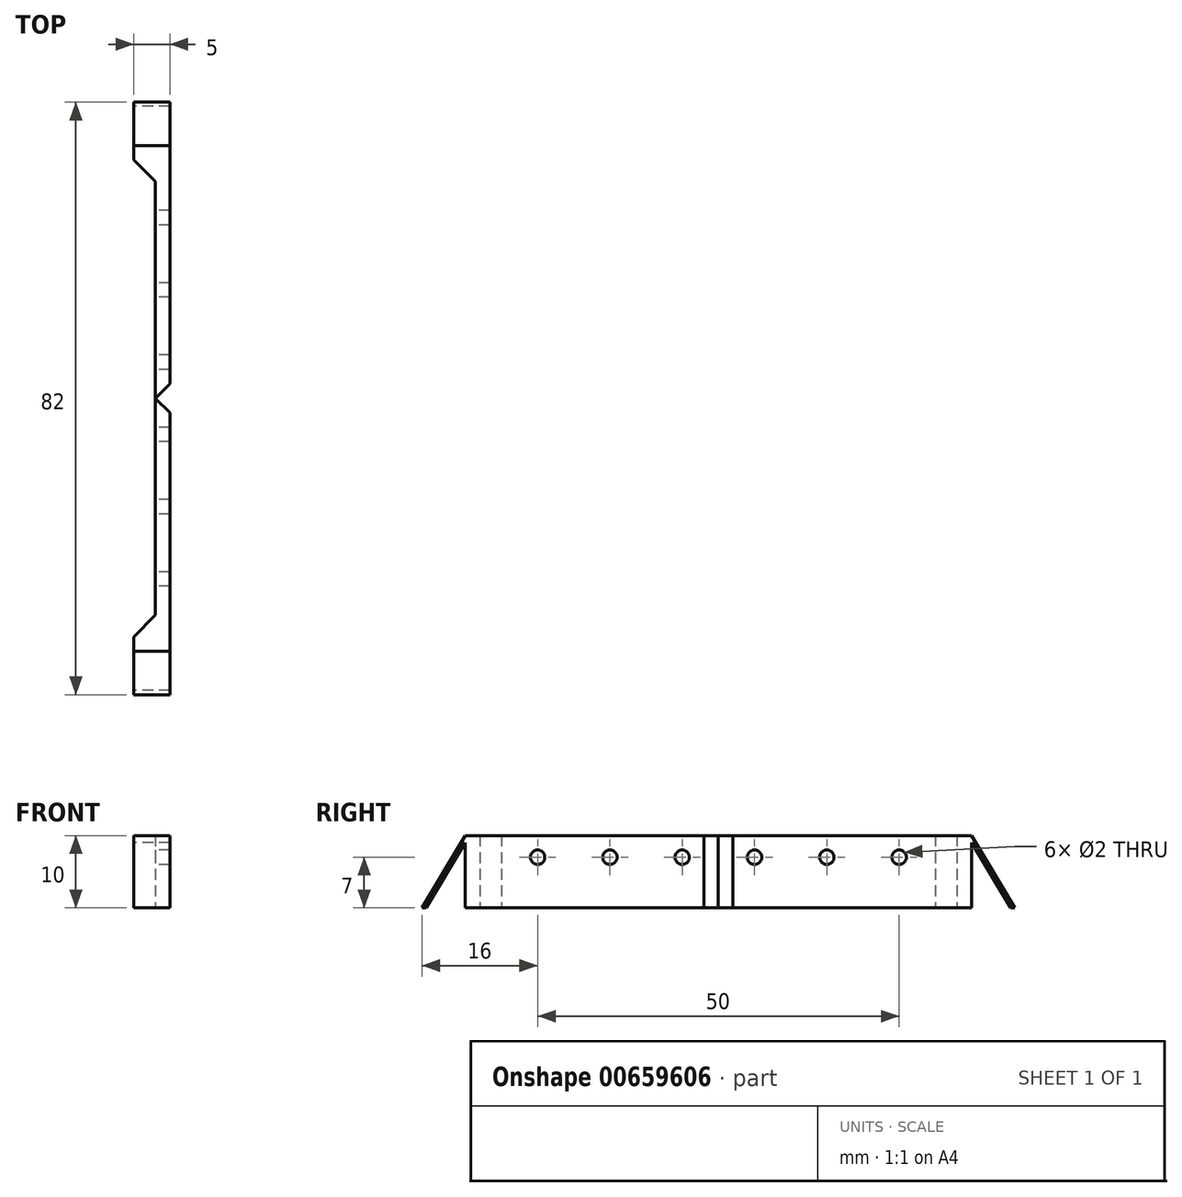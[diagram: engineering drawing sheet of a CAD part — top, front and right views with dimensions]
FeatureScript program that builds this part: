
annotation { "Feature Type Name" : "Feature", "Feature Type Description" : "" }
export const myFeature = defineFeature(function(context is Context, id is Id, definition is map)
    precondition{}
    {
        {
            var Q0;
            Q0=qCreatedBy(makeId("Top.planeOp"),FACE);
            var sketch = newSketch(context, id + "F0", { "sketchPlane" : qUnion([Q0])});
            skLineSegment(sketch, "E0.bottom", {"start": v(20, -19.5) * mm, "end": v(-20, -19.5) * mm});
            skLineSegment(sketch, "E0.top", {"start": v(20, 19.5) * mm, "end": v(-20, 19.5) * mm});
            skLineSegment(sketch, "E0.left", {"start": v(20, -19.5) * mm, "end": v(20, 19.5) * mm});
            skLineSegment(sketch, "E0.right", {"start": v(-20, -19.5) * mm, "end": v(-20, 19.5) * mm});
            skPoint(sketch, "E0.middle", {"position": v(0, 0) * mm});
            skLineSegment(sketch, "E1.0", {"start": v(22, -21.5) * mm, "end": v(-22, -21.5) * mm});
            skLineSegment(sketch, "E1.1", {"start": v(22, -21.5) * mm, "end": v(22, 21.5) * mm});
            skLineSegment(sketch, "E1.2", {"start": v(22, 21.5) * mm, "end": v(-22, 21.5) * mm});
            skLineSegment(sketch, "E1.3", {"start": v(-22, -21.5) * mm, "end": v(-22, 21.5) * mm});
            skLineSegment(sketch, "E2", {"start": v(-20, -19.5) * mm, "end": v(-22, -19.5) * mm});
            skLineSegment(sketch, "E3", {"start": v(20, 19.5) * mm, "end": v(20, 21.5) * mm});
            skSolve(sketch);
        }
        {
            var Q0;
            Q0=makeQuery(id+"F0.imprint","IMPRINT",FACE,{"disambiguationData":[TD([[makeQuery(id+"F0.imprint","IMPRINT",EDGE,{"derivedFrom":sQuery(id+"F0.wireOp",EDGE,"E0.top")}),-1.0]])]});
            var Q1;
            Q1=makeQuery(id+"F0.imprint","IMPRINT",FACE,{"disambiguationData":[TD([[makeQuery(id+"F0.imprint","IMPRINT",EDGE,{"derivedFrom":sQuery(id+"F0.wireOp",EDGE,"E0.bottom")}),1.0]])]});
            extrude(context, id + "F1", {"entities" : qUnion([Q0, Q1]), "oppositeDirection" : true, "depth" : 10 * mm, "offsetDistance" : 25 * mm});
        }
        {
            var Q0;
            Q0=makeQuery(id+"F1.opExtrude","SWEPT_FACE",FACE,{"disambiguationData":[OSD([sQuery(id+"F0.wireOp",EDGE,"E1.3")])]});
            var sketch = newSketch(context, id + "F2", { "sketchPlane" : qUnion([Q0])});
            skLineSegment(sketch, "E4", {"start": v(13.5, 0) * mm, "end": v(19.5, -10) * mm});
            skLineSegment(sketch, "E5", {"start": v(19.5, -10) * mm, "end": v(18.92, -10) * mm});
            skLineSegment(sketch, "E6", {"start": v(18.92, -10) * mm, "end": v(13.5, -0.97) * mm});
            skLineSegment(sketch, "E7", {"start": v(13.5, -0.97) * mm, "end": v(13.5, -10) * mm});
            skLineSegment(sketch, "E8", {"start": v(19.5, -10) * mm, "end": v(19.5, 0) * mm});
            skLineSegment(sketch, "E9", {"start": v(19.5, 0) * mm, "end": v(13.5, 0) * mm});
            skSolve(sketch);
        }
        {
            var Q0;
            {var subQ0=sQuery(id+"F2.wireOp",EDGE,"E6");Q0=makeQuery(id+"F2.imprint","IMPRINT",FACE,{"disambiguationData":[TD([[makeQuery(id+"F2.imprint","IMPRINT",EDGE,{"derivedFrom":subQ0}),1.0]])]});}
            extrude(context, id + "F3", {"entities" : qUnion([Q0]), "operationType" : NewBodyOperationType.REMOVE, "oppositeDirection" : true, "depth" : 25 * mm, "offsetDistance" : 25 * mm});
        }
        {
            var Q0;
            Q0=makeQuery(id+"F2.imprint","IMPRINT",FACE,{"disambiguationData":[TD([[makeQuery(id+"F2.imprint","IMPRINT",EDGE,{"derivedFrom":sQuery(id+"F2.wireOp",EDGE,"E4")}),1.0]])]});
            extrude(context, id + "F4", {"entities" : qUnion([Q0]), "operationType" : NewBodyOperationType.REMOVE, "endBound" : BoundingType.THROUGH_ALL, "oppositeDirection" : true, "depth" : 2 * mm, "offsetDistance" : 25 * mm});
        }
        {
            var Q0;
            Q0=makeQuery(id+"F1.opExtrude","SWEPT_FACE",FACE,{"disambiguationData":[OSD([sQuery(id+"F0.wireOp",EDGE,"E1.2")])]});
            var sketch = newSketch(context, id + "F5", { "sketchPlane" : qUnion([Q0])});
            skLineSegment(sketch, "E10", {"start": v(-20, -10) * mm, "end": v(-14, -0.9) * mm});
            skLineSegment(sketch, "E11", {"start": v(-14, -0.9) * mm, "end": v(-14, -10) * mm});
            skLineSegment(sketch, "E12", {"start": v(-14, 0) * mm, "end": v(-20, -9.1) * mm});
            skLineSegment(sketch, "E13", {"start": v(-20, -9.1) * mm, "end": v(-20, -10) * mm});
            skSolve(sketch);
        }
        {
            var Q0;
            {var subQ0=sQuery(id+"F5.wireOp",EDGE,"E10");Q0=makeQuery(id+"F5.imprint","IMPRINT",FACE,{"disambiguationData":[TD([[makeQuery(id+"F5.imprint","IMPRINT",EDGE,{"derivedFrom":subQ0}),-1.0]])]});}
            var Q1;
            {var subQ3=sQuery(id+"F5.wireOp",EDGE,"E12");Q1=makeQuery(id+"F5.imprint","IMPRINT",FACE,{"disambiguationData":[TD([[makeQuery(id+"F5.imprint","IMPRINT",EDGE,{"derivedFrom":subQ3}),-1.0]])]});}
            extrude(context, id + "F6", {"entities" : qUnion([Q0, Q1]), "operationType" : NewBodyOperationType.REMOVE, "endBound" : BoundingType.THROUGH_ALL, "oppositeDirection" : true, "depth" : 25 * mm, "offsetDistance" : 25 * mm});
        }
        {
            var Q0;
            {var subQ0=sQuery(id+"F0.wireOp",EDGE,"E1.3");var subQ7=sQuery(id+"F0.wireOp",EDGE,"E0.bottom");Q0=makeQuery(id+"F4.boolean.opBoolean","SPLIT",FACE,{"disambiguationData":[TD([makeQuery(id+"F1.opExtrude","SWEPT_FACE",FACE,{"disambiguationData":[OSD([subQ7])]})])],"derivedFrom":makeQuery(id+"F1.opExtrude","SWEPT_FACE",FACE,{"disambiguationData":[OSD([subQ0])]})});}
            extrude(context, id + "F7", {"entities" : qUnion([Q0]), "operationType" : NewBodyOperationType.REMOVE, "endBound" : BoundingType.THROUGH_ALL, "oppositeDirection" : true, "depth" : 25 * mm, "offsetDistance" : 25 * mm});
        }
        {
            var Q0;
            Q0=makeQuery(id+"F1.opExtrude","SWEPT_FACE",FACE,{"disambiguationData":[OSD([sQuery(id+"F0.wireOp",EDGE,"E1.2")])]});
            var sketch = newSketch(context, id + "F8", { "sketchPlane" : qUnion([Q0])});
            skLineSegment(sketch, "E14", {"start": v(-9, -10) * mm, "end": v(-9, 0) * mm});
            skSolve(sketch);
        }
        {
            var Q0;
            {var subQ2=sQuery(id+"F8.wireOp",EDGE,"E14");Q0=makeQuery(id+"F8.imprint","IMPRINT",FACE,{"disambiguationData":[TD([[makeQuery(id+"F8.imprint","IMPRINT",EDGE,{"derivedFrom":subQ2}),1.0]])]});}
            extrude(context, id + "F9", {"entities" : qUnion([Q0]), "operationType" : NewBodyOperationType.ADD, "depth" : 3 * mm, "offsetDistance" : 25 * mm});
        }
        {
            var Q0;
            Q0=makeQuery(id+"F9.opExtrude","CAP_EDGE",EDGE,{"disambiguationData":[OSD([sQuery(id+"F8.wireOp",EDGE,"E14")])],"isStart":false});
            chamfer(context, id + "F10", {"entities" : qUnion([Q0]), "width" : 3 * mm, "tangentPropagation" : true});
        }
        {
            var Q0;
            {var subQ0=sQuery(id+"F0.wireOp",EDGE,"E1.2");var subQ1=sQuery(id+"F0.wireOp",EDGE,"E1.3");Q0=makeQuery(id+"F4.boolean.opBoolean","SPLIT",FACE,{"disambiguationData":[TD([makeQuery(id+"F1.opExtrude","SWEPT_FACE",FACE,{"disambiguationData":[OSD([subQ0])]})])],"derivedFrom":makeQuery(id+"F1.opExtrude","SWEPT_FACE",FACE,{"disambiguationData":[OSD([subQ1])]})});}
            var sketch = newSketch(context, id + "F11", { "sketchPlane" : qUnion([Q0])});
            skLineSegment(sketch, "E15", {"start": v(8.5, 0) * mm, "end": v(8.5, -10) * mm});
            skSolve(sketch);
        }
        {
            var Q0;
            {var subQ5=sQuery(id+"F11.wireOp",EDGE,"E15");Q0=makeQuery(id+"F11.imprint","IMPRINT",FACE,{"disambiguationData":[TD([[makeQuery(id+"F11.imprint","IMPRINT",EDGE,{"derivedFrom":subQ5}),1.0]])]});}
            extrude(context, id + "F12", {"entities" : qUnion([Q0]), "operationType" : NewBodyOperationType.ADD, "depth" : 3 * mm, "offsetDistance" : 25 * mm});
        }
        {
            var Q0;
            Q0=makeQuery(id+"F12.opExtrude","CAP_EDGE",EDGE,{"disambiguationData":[OSD([sQuery(id+"F11.wireOp",EDGE,"E15")])],"isStart":false});
            chamfer(context, id + "F13", {"entities" : qUnion([Q0]), "width" : 3 * mm, "tangentPropagation" : true});
        }
        {
            var Q0;
            {var subQ0=sQuery(id+"F0.wireOp",EDGE,"E1.2");var subQ1=sQuery(id+"F0.wireOp",EDGE,"E1.3");Q0=makeQuery(id+"F4.boolean.opBoolean","SPLIT",FACE,{"disambiguationData":[TD([makeQuery(id+"F1.opExtrude","SWEPT_FACE",FACE,{"disambiguationData":[OSD([subQ0])]})])],"derivedFrom":makeQuery(id+"F1.opExtrude","SWEPT_FACE",FACE,{"disambiguationData":[OSD([subQ1])]})});}
            var sketch = newSketch(context, id + "F14", { "sketchPlane" : qUnion([Q0])});
            skLineSegment(sketch, "E16", {"start": v(-6.5, -10) * mm, "end": v(-6.5, -3) * mm, "construction": true});
            skPoint(sketch, "E16.endSnap0", {"position": v(-6.5, -10) * mm});
            skLineSegment(sketch, "E17", {"start": v(-6.5, -3) * mm, "end": v(3.5, -3) * mm, "construction": true});
            skLineSegment(sketch, "E18", {"start": v(-6.5, -3) * mm, "end": v(-16.5, -3) * mm, "construction": true});
            skSolve(sketch);
        }
        {
            var Q0;
            Q0=makeQuery(id+"F1.opExtrude","SWEPT_FACE",FACE,{"disambiguationData":[OSD([sQuery(id+"F0.wireOp",EDGE,"E1.2")])]});
            var sketch = newSketch(context, id + "F15", { "sketchPlane" : qUnion([Q0])});
            skLineSegment(sketch, "E19", {"start": v(6.5, -3) * mm, "end": v(16.5, -3) * mm, "construction": true});
            skPoint(sketch, "E19.startSnap0", {"position": v(6.5, -10) * mm});
            skLineSegment(sketch, "E20", {"start": v(6.5, -3) * mm, "end": v(-3.5, -3) * mm, "construction": true});
            skLineSegment(sketch, "E21", {"start": v(6.5, -3) * mm, "end": v(6.5, -10) * mm, "construction": true});
            skSolve(sketch);
        }
        {
            var Q0;
            Q0=sQuery(id+"F14.wireOp",VERTEX,"E18.start");
            var Q1;
            Q1=sQuery(id+"F14.wireOp",VERTEX,"E17.end");
            var Q2;
            Q2=sQuery(id+"F14.wireOp",VERTEX,"E18.end");
            var Q3;
            Q3=makeQuery(id+"F4.boolean.opBoolean","SPLIT",BODY,{"disambiguationData":[OD(1.0)],"derivedFrom":makeQuery(id+"F1.opExtrude","SWEPT_BODY",BODY,{"disambiguationData":[OSD([sQuery(id+"F0.wireOp",EDGE,"E0.bottom"),sQuery(id+"F0.wireOp",EDGE,"E0.top"),sQuery(id+"F0.wireOp",EDGE,"E0.left"),sQuery(id+"F0.wireOp",EDGE,"E0.right"),sQuery(id+"F0.wireOp",EDGE,"E1.0"),sQuery(id+"F0.wireOp",EDGE,"E1.1"),sQuery(id+"F0.wireOp",EDGE,"E1.2"),sQuery(id+"F0.wireOp",EDGE,"E1.3")])]})});
            hole(context, id + "F16", {"style" : HoleStyle.SIMPLE, "endStyle" : HoleEndStyle.THROUGH, "holeDiameter" : 2 * mm, "majorDiameter" : 5 * mm, "isTappedThrough" : true, "tappedDepth" : 12 * mm, "tapClearance" : 3, "locations" : qUnion([Q0, Q1, Q2]), "scope" : qUnion([Q3])});
        }
        {
            var Q0;
            Q0=sQuery(id+"F15.wireOp",VERTEX,"E20.end");
            var Q1;
            Q1=sQuery(id+"F15.wireOp",VERTEX,"E19.start");
            var Q2;
            Q2=sQuery(id+"F15.wireOp",VERTEX,"E19.end");
            var Q3;
            Q3=makeQuery(id+"F4.boolean.opBoolean","SPLIT",BODY,{"disambiguationData":[OD(1.0)],"derivedFrom":makeQuery(id+"F1.opExtrude","SWEPT_BODY",BODY,{"disambiguationData":[OSD([sQuery(id+"F0.wireOp",EDGE,"E0.bottom"),sQuery(id+"F0.wireOp",EDGE,"E0.top"),sQuery(id+"F0.wireOp",EDGE,"E0.left"),sQuery(id+"F0.wireOp",EDGE,"E0.right"),sQuery(id+"F0.wireOp",EDGE,"E1.0"),sQuery(id+"F0.wireOp",EDGE,"E1.1"),sQuery(id+"F0.wireOp",EDGE,"E1.2"),sQuery(id+"F0.wireOp",EDGE,"E1.3")])]})});
            hole(context, id + "F17", {"style" : HoleStyle.SIMPLE, "endStyle" : HoleEndStyle.THROUGH, "holeDiameter" : 2 * mm, "majorDiameter" : 5 * mm, "isTappedThrough" : true, "tappedDepth" : 12 * mm, "tapClearance" : 3, "locations" : qUnion([Q0, Q1, Q2]), "scope" : qUnion([Q3])});
        }
        {
            var Q0;
            Q0=makeQuery(id+"F1.opExtrude","SWEPT_FACE",FACE,{"disambiguationData":[OSD([sQuery(id+"F0.wireOp",EDGE,"E0.top")])]});
            extrude(context, id + "F18", {"entities" : qUnion([Q0]), "operationType" : NewBodyOperationType.REMOVE, "oppositeDirection" : true, "depth" : 25 * mm, "offsetDistance" : 25 * mm});
        }
        {
            var Q0;
            Q0=makeQuery(id+"F4.boolean.opBoolean","SPLIT",BODY,{"disambiguationData":[OD(1.0)],"derivedFrom":makeQuery(id+"F1.opExtrude","SWEPT_BODY",BODY,{"disambiguationData":[OSD([sQuery(id+"F0.wireOp",EDGE,"E0.bottom"),sQuery(id+"F0.wireOp",EDGE,"E0.top"),sQuery(id+"F0.wireOp",EDGE,"E0.left"),sQuery(id+"F0.wireOp",EDGE,"E0.right"),sQuery(id+"F0.wireOp",EDGE,"E1.0"),sQuery(id+"F0.wireOp",EDGE,"E1.1"),sQuery(id+"F0.wireOp",EDGE,"E1.2"),sQuery(id+"F0.wireOp",EDGE,"E1.3")])]})});
            var Q1;
            Q1=makeQuery(id+"F1.opExtrude","SWEPT_FACE",FACE,{"disambiguationData":[OSD([sQuery(id+"F0.wireOp",EDGE,"E1.2")])]});
            mirror(context, id + "F19", {"operationType" : NewBodyOperationType.ADD, "entities" : qUnion([Q0]), "mirrorPlane" : qUnion([Q1])});
        }
        {
            var Q0;
            {var subQ0=sQuery(id+"F0.wireOp",EDGE,"E1.3");var subQ1=sQuery(id+"F0.wireOp",EDGE,"E1.2");var subQ2=sQuery(id+"F0.wireOp",EDGE,"E1.1");var subQ3=sQuery(id+"F0.wireOp",EDGE,"E0.right");var subQ4=sQuery(id+"F0.wireOp",EDGE,"E0.left");var subQ5=sQuery(id+"F0.wireOp",EDGE,"E0.top");var subQ6=makeQuery(id+"F1.opExtrude","CAP_FACE",FACE,{"disambiguationData":[OSD([sQuery(id+"F0.wireOp",EDGE,"E0.bottom"),subQ5,subQ4,subQ3,sQuery(id+"F0.wireOp",EDGE,"E1.0"),subQ2,subQ1,subQ0])],"isStart":true});var subQ7=makeQuery(id+"F1.opExtrude","SWEPT_FACE",FACE,{"disambiguationData":[OSD([subQ1])]});var subQ9=sQuery(id+"F2.wireOp",EDGE,"E4");var subQ11=makeQuery(id+"F4.boolean.opBoolean","SPLIT",EDGE,{"disambiguationData":[TD([subQ7])],"derivedFrom":makeQuery(id+"F1.opExtrude","CAP_EDGE",EDGE,{"disambiguationData":[OSD([subQ0])],"isStart":true})});var subQ12=makeQuery(id+"F1.opExtrude","CAP_EDGE",EDGE,{"disambiguationData":[OSD([subQ1])],"isStart":true});var subQ13=makeQuery(id+"F12.boolean.opBoolean","MERGE",FACE,{"derivedFrom":[makeQuery(id+"F9.boolean.opBoolean","MERGE",FACE,{"derivedFrom":[makeQuery(id+"F4.boolean.opBoolean","SPLIT",FACE,{"disambiguationData":[TD([makeQuery(id+"F1.opExtrude","SWEPT_FACE",FACE,{"disambiguationData":[OSD([subQ5])]})])],"derivedFrom":subQ6}),makeQuery(id+"F9.opExtrude","SWEPT_FACE",FACE,{"disambiguationData":[OSD([subQ1]),TDD([makeQuery(id+"F8.imprint","IMPRINT",EDGE,{"disambiguationData":[TD([[makeQuery(id+"F8.imprint","INTERSECT",VERTEX,{"derivedFrom":[makeQuery(id+"F6.boolean.opBoolean","COPY",EDGE,{"derivedFrom":makeQuery(id+"F6.opExtrude","CAP_EDGE",EDGE,{"disambiguationData":[OSD([sQuery(id+"F5.wireOp",EDGE,"E12")])],"isStart":true})}),subQ12]}),-1.0]])],"derivedFrom":subQ12})])]})]}),makeQuery(id+"F12.opExtrude","SWEPT_FACE",FACE,{"disambiguationData":[OSD([subQ0]),TDD([makeQuery(id+"F11.imprint","IMPRINT",EDGE,{"disambiguationData":[TD([[makeQuery(id+"F11.imprint","INTERSECT",VERTEX,{"derivedFrom":[makeQuery(id+"F4.boolean.opBoolean","COPY",EDGE,{"derivedFrom":makeQuery(id+"F4.opExtrude","CAP_EDGE",EDGE,{"disambiguationData":[OSD([subQ9])],"isStart":true})}),subQ11]}),-1.0]])],"derivedFrom":subQ11})])]})]});Q0=makeQuery(id+"F19.boolean.opBoolean","MERGE",FACE,{"derivedFrom":[subQ13,makeQuery(id+"F19.opPattern","COPY",FACE,{"derivedFrom":subQ13,"instanceName":"1"})]});}
            var sketch = newSketch(context, id + "F20", { "sketchPlane" : qUnion([Q0])});
            skLineSegment(sketch, "E22", {"start": v(-22, 21.5) * mm, "end": v(-20, 19.5) * mm});
            skLineSegment(sketch, "E23", {"start": v(-22, 21.5) * mm, "end": v(-20, 23.5) * mm});
            skSolve(sketch);
        }
        {
            var Q0;
            {var subQ0=sQuery(id+"F20.wireOp",EDGE,"E22");Q0=makeQuery(id+"F20.imprint","IMPRINT",FACE,{"disambiguationData":[TD([[makeQuery(id+"F20.imprint","IMPRINT",EDGE,{"derivedFrom":subQ0}),1.0]])]});}
            extrude(context, id + "F21", {"entities" : qUnion([Q0]), "operationType" : NewBodyOperationType.REMOVE, "oppositeDirection" : true, "depth" : 25 * mm, "offsetDistance" : 25 * mm});
        }
    });
